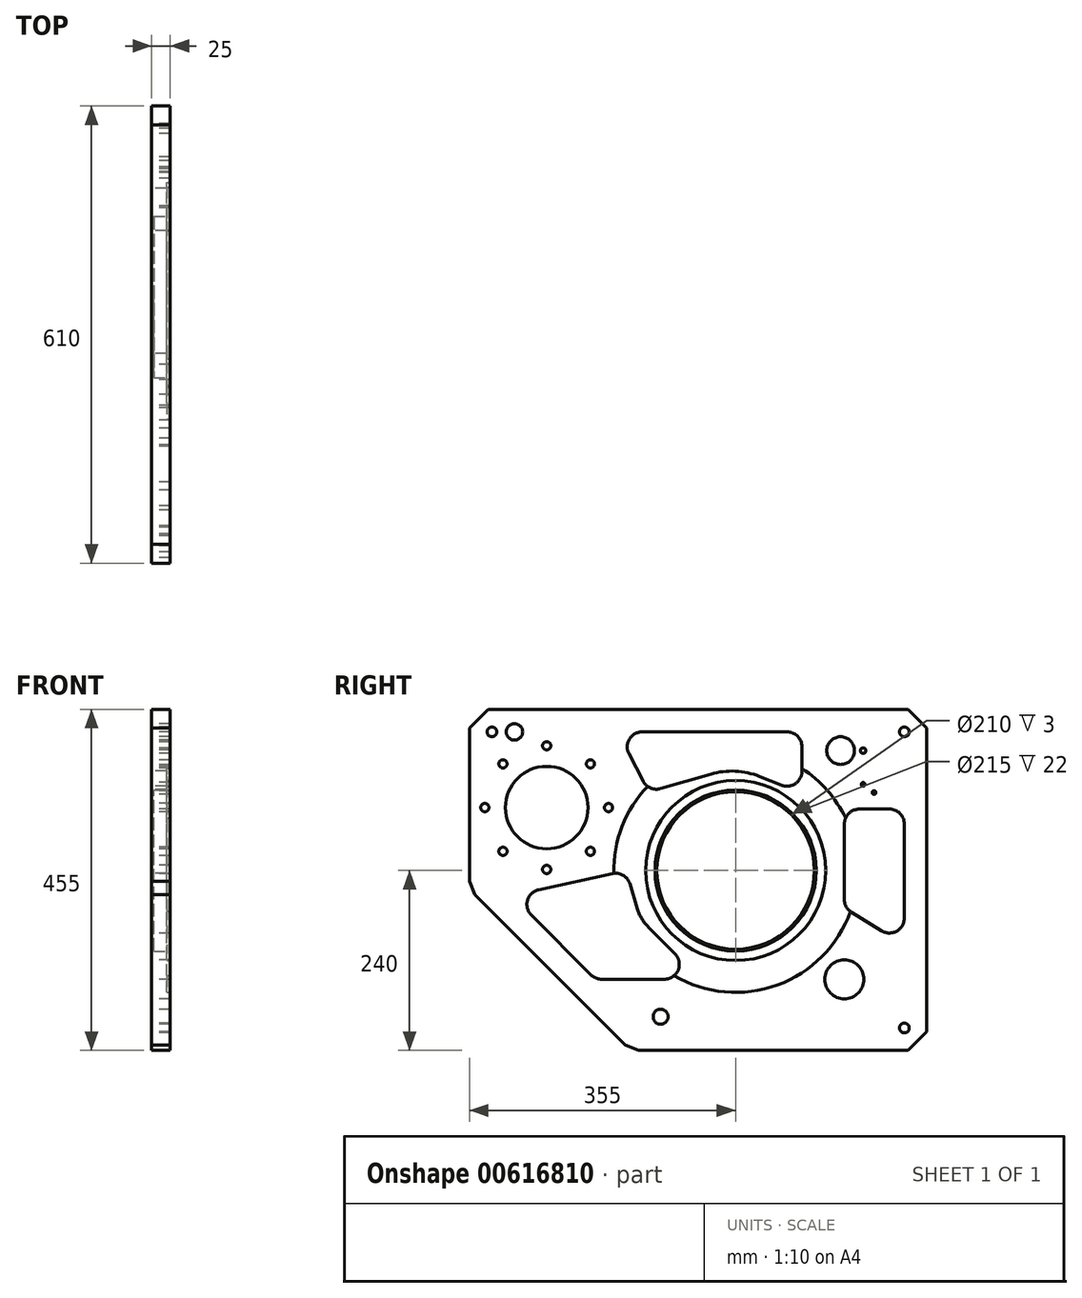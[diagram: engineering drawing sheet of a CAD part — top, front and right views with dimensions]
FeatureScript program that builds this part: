
annotation { "Feature Type Name" : "Feature", "Feature Type Description" : "" }
export const myFeature = defineFeature(function(context is Context, id is Id, definition is map)
    precondition{}
    {
        {
            var Q0;
            Q0=qCreatedBy(makeId("Right.planeOp"),FACE);
            var sketch = newSketch(context, id + "F0", { "sketchPlane" : qUnion([Q0])});
            skCircle(sketch, "E0", {"center": v(225, 185) * mm, "radius": 6.5 * mm});
            skCircle(sketch, "E1", {"center": v(225, -210) * mm, "radius": 6.5 * mm});
            skCircle(sketch, "E2", {"center": v(-100, -195) * mm, "radius": 10 * mm});
            skCircle(sketch, "E3", {"center": v(-325, 185) * mm, "radius": 6.5 * mm});
            skCircle(sketch, "E4", {"center": v(-295, 185) * mm, "radius": 11 * mm});
            skCircle(sketch, "E5", {"center": v(-252, 84) * mm, "radius": 20 * mm});
            skLineSegment(sketch, "E6", {"start": v(-147.32, -232.68) * mm, "end": v(-347.68, -32.32) * mm, "construction": true});
            skLineSegment(sketch, "E7", {"start": v(-355, -14.64) * mm, "end": v(-355, 190) * mm, "construction": true});
            skCircle(sketch, "E8", {"center": v(145, -145) * mm, "radius": 26 * mm});
            skLineSegment(sketch, "E9", {"start": v(255, 190) * mm, "end": v(255, -215) * mm, "construction": true});
            skLineSegment(sketch, "E10", {"start": v(230, 215) * mm, "end": v(-330, 215) * mm, "construction": true});
            skLineSegment(sketch, "E11", {"start": v(-129.64, -240) * mm, "end": v(230, -240) * mm, "construction": true});
            skCircle(sketch, "E12", {"center": v(140, 160) * mm, "radius": 18.5 * mm});
            skCircle(sketch, "E13", {"center": v(0, 0) * mm, "radius": 105 * mm});
            skCircle(sketch, "E14", {"center": v(177, -160) * mm, "radius": 9 * mm, "construction": true});
            skLineSegment(sketch, "E15", {"start": v(255, 190) * mm, "end": v(255, -215) * mm});
            skLineSegment(sketch, "E16", {"start": v(255, -215) * mm, "end": v(230, -240) * mm});
            skLineSegment(sketch, "E17", {"start": v(-129.64, -240) * mm, "end": v(230, -240) * mm});
            skLineSegment(sketch, "E18", {"start": v(-129.64, -240) * mm, "end": v(-147.32, -232.68) * mm});
            skLineSegment(sketch, "E19", {"start": v(-147.32, -232.68) * mm, "end": v(-347.68, -32.32) * mm});
            skLineSegment(sketch, "E20", {"start": v(-347.68, -32.32) * mm, "end": v(-355, -14.64) * mm});
            skLineSegment(sketch, "E21", {"start": v(-355, -14.64) * mm, "end": v(-355, 190) * mm});
            skLineSegment(sketch, "E22", {"start": v(-355, 190) * mm, "end": v(-330, 215) * mm});
            skLineSegment(sketch, "E23", {"start": v(-330, 215) * mm, "end": v(230, 215) * mm});
            skLineSegment(sketch, "E24", {"start": v(230, 215) * mm, "end": v(255, 190) * mm});
            skCircle(sketch, "E25", {"center": v(-252, 84) * mm, "radius": 55 * mm});
            skCircle(sketch, "E26", {"center": v(-252, 84) * mm, "radius": 82.5 * mm, "construction": true});
            skCircle(sketch, "E27", {"center": v(-169.5, 84) * mm, "radius": 5.5 * mm});
            skCircle(sketch, "E28.1.0", {"center": v(-193.66, 142.34) * mm, "radius": 5.5 * mm});
            skCircle(sketch, "E28.2.0", {"center": v(-252, 166.5) * mm, "radius": 5.5 * mm});
            skCircle(sketch, "E28.3.0", {"center": v(-310.34, 142.34) * mm, "radius": 5.5 * mm});
            skCircle(sketch, "E28.4.0", {"center": v(-334.5, 84) * mm, "radius": 5.5 * mm});
            skCircle(sketch, "E28.5.0", {"center": v(-310.34, 25.66) * mm, "radius": 5.5 * mm});
            skCircle(sketch, "E28.6.0", {"center": v(-252, 1.5) * mm, "radius": 5.5 * mm});
            skCircle(sketch, "E28.7.0", {"center": v(-193.66, 25.66) * mm, "radius": 5.5 * mm});
            skCircle(sketch, "E29", {"center": v(170, 160) * mm, "radius": 3.75 * mm});
            skLineSegment(sketch, "E30", {"start": v(140, 160) * mm, "end": v(170, 160) * mm, "construction": true});
            skCircle(sketch, "E31", {"center": v(170, 115) * mm, "radius": 2.5 * mm});
            skCircle(sketch, "E32", {"center": v(184.55, 104.13) * mm, "radius": 2.5 * mm});
            skLineSegment(sketch, "E33", {"start": v(68.44, 185) * mm, "end": v(-124.6, 185) * mm});
            skLineSegment(sketch, "E34", {"start": v(-142.34, 155.76) * mm, "end": v(-123.3, 119.2) * mm});
            skLineSegment(sketch, "E35", {"start": v(-99.97, 109.23) * mm, "end": v(-33.08, 128.71) * mm});
            skLineSegment(sketch, "E36", {"start": v(31.99, 125.56) * mm, "end": v(61.01, 113.96) * mm});
            skLineSegment(sketch, "E37", {"start": v(88.44, 132.53) * mm, "end": v(88.44, 165) * mm});
            skPoint(sketch, "E38.visualSharp", {"position": v(88.44, 103) * mm});
            skArc(sketch, "E38.filletArc", {"start": v(61.01, 113.96) * mm, "mid": v(79.65, 115.97) * mm, "end": v(88.44, 132.53) * mm});
            skPoint(sketch, "E39.visualSharp", {"position": v(88.44, 185) * mm});
            skArc(sketch, "E39.filletArc", {"start": v(88.44, 165) * mm, "mid": v(82.58, 179.14) * mm, "end": v(68.44, 185) * mm});
            skPoint(sketch, "E40.visualSharp", {"position": v(-157.56, 185) * mm});
            skArc(sketch, "E40.filletArc", {"start": v(-124.6, 185) * mm, "mid": v(-141.7, 175.37) * mm, "end": v(-142.34, 155.76) * mm});
            skPoint(sketch, "E41.visualSharp", {"position": v(-115.73, 104.65) * mm});
            skArc(sketch, "E41.filletArc", {"start": v(-123.3, 119.2) * mm, "mid": v(-113.42, 110.04) * mm, "end": v(-99.97, 109.23) * mm});
            skPoint(sketch, "E42.visualSharp", {"position": v(0, 138.34) * mm});
            skArc(sketch, "E42.filletArc", {"start": v(31.99, 125.56) * mm, "mid": v(-0.28, 132.58) * mm, "end": v(-33.08, 128.71) * mm});
            skLineSegment(sketch, "E43", {"start": v(225, 62) * mm, "end": v(225, -63.36) * mm});
            skLineSegment(sketch, "E44", {"start": v(194.44, -80.34) * mm, "end": v(154.44, -55.46) * mm});
            skLineSegment(sketch, "E45", {"start": v(145, -38.48) * mm, "end": v(145, 62) * mm});
            skLineSegment(sketch, "E46", {"start": v(165, 82) * mm, "end": v(205, 82) * mm});
            skPoint(sketch, "E47.visualSharp", {"position": v(225, 82) * mm});
            skArc(sketch, "E47.filletArc", {"start": v(225, 62) * mm, "mid": v(219.14, 76.14) * mm, "end": v(205, 82) * mm});
            skPoint(sketch, "E48.visualSharp", {"position": v(145, 82) * mm});
            skArc(sketch, "E48.filletArc", {"start": v(165, 82) * mm, "mid": v(150.86, 76.14) * mm, "end": v(145, 62) * mm});
            skPoint(sketch, "E49.visualSharp", {"position": v(225, -99.36) * mm});
            skArc(sketch, "E49.filletArc", {"start": v(194.44, -80.34) * mm, "mid": v(214.71, -80.84) * mm, "end": v(225, -63.36) * mm});
            skPoint(sketch, "E50.visualSharp", {"position": v(145, -49.6) * mm});
            skArc(sketch, "E50.filletArc", {"start": v(145, -38.48) * mm, "mid": v(147.52, -48.2) * mm, "end": v(154.44, -55.46) * mm});
            skLineSegment(sketch, "E51", {"start": v(-192.72, -139.14) * mm, "end": v(-272.55, -59.31) * mm});
            skLineSegment(sketch, "E52", {"start": v(-262.71, -25.64) * mm, "end": v(-164.6, -4) * mm});
            skLineSegment(sketch, "E53", {"start": v(-141.15, -17.73) * mm, "end": v(-131.22, -50.58) * mm});
            skLineSegment(sketch, "E54", {"start": v(-116.21, -75.65) * mm, "end": v(-81, -110.86) * mm});
            skLineSegment(sketch, "E55", {"start": v(-95.14, -145) * mm, "end": v(-178.57, -145) * mm});
            skPoint(sketch, "E56.visualSharp", {"position": v(-186.86, -145) * mm});
            skArc(sketch, "E56.filletArc", {"start": v(-192.72, -139.14) * mm, "mid": v(-186.23, -143.48) * mm, "end": v(-178.57, -145) * mm});
            skPoint(sketch, "E57.visualSharp", {"position": v(-46.86, -145) * mm});
            skArc(sketch, "E57.filletArc", {"start": v(-95.14, -145) * mm, "mid": v(-76.67, -132.65) * mm, "end": v(-81, -110.86) * mm});
            skPoint(sketch, "E58.visualSharp", {"position": v(-298.35, -33.5) * mm});
            skArc(sketch, "E58.filletArc", {"start": v(-262.71, -25.64) * mm, "mid": v(-277.6, -39.56) * mm, "end": v(-272.55, -59.31) * mm});
            skPoint(sketch, "E59.visualSharp", {"position": v(-146.5, 0) * mm});
            skArc(sketch, "E59.filletArc", {"start": v(-141.15, -17.73) * mm, "mid": v(-150.18, -6.27) * mm, "end": v(-164.6, -4) * mm});
            skPoint(sketch, "E60.visualSharp", {"position": v(-126.86, -65) * mm});
            skArc(sketch, "E60.filletArc", {"start": v(-131.22, -50.58) * mm, "mid": v(-125.26, -64.04) * mm, "end": v(-116.21, -75.65) * mm});
            skSolve(sketch);
        }
        {
            var Q0;
            Q0 = qSketchRegion(id + "F0", true);
            extrude(context, id + "F1", {"entities" : qUnion([Q0]), "depth" : 25 * mm, "offsetDistance" : 25 * mm});
        }
        {
            var Q0;
            Q0=makeQuery(id+"F1.opExtrude","CAP_FACE",FACE,{"disambiguationData":[OSD([sQuery(id+"F0.wireOp",EDGE,"c79e81bd-bfa4-4131-aa7d-9b8266e86020"),sQuery(id+"F0.wireOp",EDGE,"E0"),sQuery(id+"F0.wireOp",EDGE,"E1"),sQuery(id+"F0.wireOp",EDGE,"E2"),sQuery(id+"F0.wireOp",EDGE,"E3"),sQuery(id+"F0.wireOp",EDGE,"E4"),sQuery(id+"F0.wireOp",EDGE,"E8"),sQuery(id+"F0.wireOp",EDGE,"E12"),sQuery(id+"F0.wireOp",EDGE,"E13"),sQuery(id+"F0.wireOp",EDGE,"E15"),sQuery(id+"F0.wireOp",EDGE,"E16"),sQuery(id+"F0.wireOp",EDGE,"E17"),sQuery(id+"F0.wireOp",EDGE,"E18"),sQuery(id+"F0.wireOp",EDGE,"E19"),sQuery(id+"F0.wireOp",EDGE,"E20"),sQuery(id+"F0.wireOp",EDGE,"E21"),sQuery(id+"F0.wireOp",EDGE,"E22"),sQuery(id+"F0.wireOp",EDGE,"E23"),sQuery(id+"F0.wireOp",EDGE,"E24"),sQuery(id+"F0.wireOp",EDGE,"E25"),sQuery(id+"F0.wireOp",EDGE,"E27"),sQuery(id+"F0.wireOp",EDGE,"E28.1.0"),sQuery(id+"F0.wireOp",EDGE,"E28.2.0"),sQuery(id+"F0.wireOp",EDGE,"E28.3.0"),sQuery(id+"F0.wireOp",EDGE,"E28.4.0"),sQuery(id+"F0.wireOp",EDGE,"E28.5.0"),sQuery(id+"F0.wireOp",EDGE,"E28.6.0"),sQuery(id+"F0.wireOp",EDGE,"E28.7.0"),sQuery(id+"F0.wireOp",EDGE,"5564e748-2a2c-4b64-980b-efb594590cff.4.0"),sQuery(id+"F0.wireOp",EDGE,"9xgvsZil-ayej-kInM-w8W6-ncIAKawD6FMf"),sQuery(id+"F0.wireOp",EDGE,"c686cf07-cc54-4e5a-8458-a5a25681e719.1.0"),sQuery(id+"F0.wireOp",EDGE,"c686cf07-cc54-4e5a-8458-a5a25681e719.2.0"),sQuery(id+"F0.wireOp",EDGE,"c686cf07-cc54-4e5a-8458-a5a25681e719.3.0"),sQuery(id+"F0.wireOp",EDGE,"c686cf07-cc54-4e5a-8458-a5a25681e719.4.0"),sQuery(id+"F0.wireOp",EDGE,"7c69ab54-7610-477c-95d2-13a8de38573c.1.0"),sQuery(id+"F0.wireOp",EDGE,"7c69ab54-7610-477c-95d2-13a8de38573c.2.0"),sQuery(id+"F0.wireOp",EDGE,"7c69ab54-7610-477c-95d2-13a8de38573c.3.0"),sQuery(id+"F0.wireOp",EDGE,"7c69ab54-7610-477c-95d2-13a8de38573c.4.0")])],"isStart":false});
            var sketch = newSketch(context, id + "F2", { "sketchPlane" : qUnion([Q0])});
            skCircle(sketch, "E61", {"center": v(0, 0) * mm, "radius": 107.5 * mm});
            skSolve(sketch);
        }
        {
            var Q0;
            Q0 = qSketchRegion(id + "F2", true);
            extrude(context, id + "F3", {"entities" : qUnion([Q0]), "operationType" : NewBodyOperationType.REMOVE, "oppositeDirection" : true, "depth" : 22 * mm, "offsetDistance" : 25 * mm});
        }
        {
            var Q0;
            Q0=makeQuery(id+"F1.opExtrude","CAP_FACE",FACE,{"disambiguationData":[OSD([sQuery(id+"F0.wireOp",EDGE,"c79e81bd-bfa4-4131-aa7d-9b8266e86020"),sQuery(id+"F0.wireOp",EDGE,"E0"),sQuery(id+"F0.wireOp",EDGE,"E1"),sQuery(id+"F0.wireOp",EDGE,"E2"),sQuery(id+"F0.wireOp",EDGE,"E3"),sQuery(id+"F0.wireOp",EDGE,"E4"),sQuery(id+"F0.wireOp",EDGE,"E8"),sQuery(id+"F0.wireOp",EDGE,"E12"),sQuery(id+"F0.wireOp",EDGE,"E13"),sQuery(id+"F0.wireOp",EDGE,"E15"),sQuery(id+"F0.wireOp",EDGE,"E16"),sQuery(id+"F0.wireOp",EDGE,"E17"),sQuery(id+"F0.wireOp",EDGE,"E18"),sQuery(id+"F0.wireOp",EDGE,"E19"),sQuery(id+"F0.wireOp",EDGE,"E20"),sQuery(id+"F0.wireOp",EDGE,"E21"),sQuery(id+"F0.wireOp",EDGE,"E22"),sQuery(id+"F0.wireOp",EDGE,"E23"),sQuery(id+"F0.wireOp",EDGE,"E24"),sQuery(id+"F0.wireOp",EDGE,"E25"),sQuery(id+"F0.wireOp",EDGE,"E27"),sQuery(id+"F0.wireOp",EDGE,"E28.1.0"),sQuery(id+"F0.wireOp",EDGE,"E28.2.0"),sQuery(id+"F0.wireOp",EDGE,"E28.3.0"),sQuery(id+"F0.wireOp",EDGE,"E28.4.0"),sQuery(id+"F0.wireOp",EDGE,"E28.5.0"),sQuery(id+"F0.wireOp",EDGE,"E28.6.0"),sQuery(id+"F0.wireOp",EDGE,"E28.7.0"),sQuery(id+"F0.wireOp",EDGE,"5564e748-2a2c-4b64-980b-efb594590cff.4.0"),sQuery(id+"F0.wireOp",EDGE,"9xgvsZil-ayej-kInM-w8W6-ncIAKawD6FMf"),sQuery(id+"F0.wireOp",EDGE,"c686cf07-cc54-4e5a-8458-a5a25681e719.1.0"),sQuery(id+"F0.wireOp",EDGE,"c686cf07-cc54-4e5a-8458-a5a25681e719.2.0"),sQuery(id+"F0.wireOp",EDGE,"c686cf07-cc54-4e5a-8458-a5a25681e719.3.0"),sQuery(id+"F0.wireOp",EDGE,"c686cf07-cc54-4e5a-8458-a5a25681e719.4.0"),sQuery(id+"F0.wireOp",EDGE,"7c69ab54-7610-477c-95d2-13a8de38573c.1.0"),sQuery(id+"F0.wireOp",EDGE,"7c69ab54-7610-477c-95d2-13a8de38573c.2.0"),sQuery(id+"F0.wireOp",EDGE,"7c69ab54-7610-477c-95d2-13a8de38573c.3.0"),sQuery(id+"F0.wireOp",EDGE,"7c69ab54-7610-477c-95d2-13a8de38573c.4.0")])],"isStart":false});
            var sketch = newSketch(context, id + "F4", { "sketchPlane" : qUnion([Q0])});
            skCircle(sketch, "E62", {"center": v(0, 0) * mm, "radius": 120 * mm});
            skCircle(sketch, "E63", {"center": v(0, 0) * mm, "radius": 162.5 * mm});
            skSolve(sketch);
        }
        {
            var Q0;
            Q0 = qSketchRegion(id + "F4", true);
            extrude(context, id + "F5", {"entities" : qUnion([Q0]), "operationType" : NewBodyOperationType.REMOVE, "oppositeDirection" : true, "depth" : 5 * mm, "offsetDistance" : 25 * mm});
        }
    });
